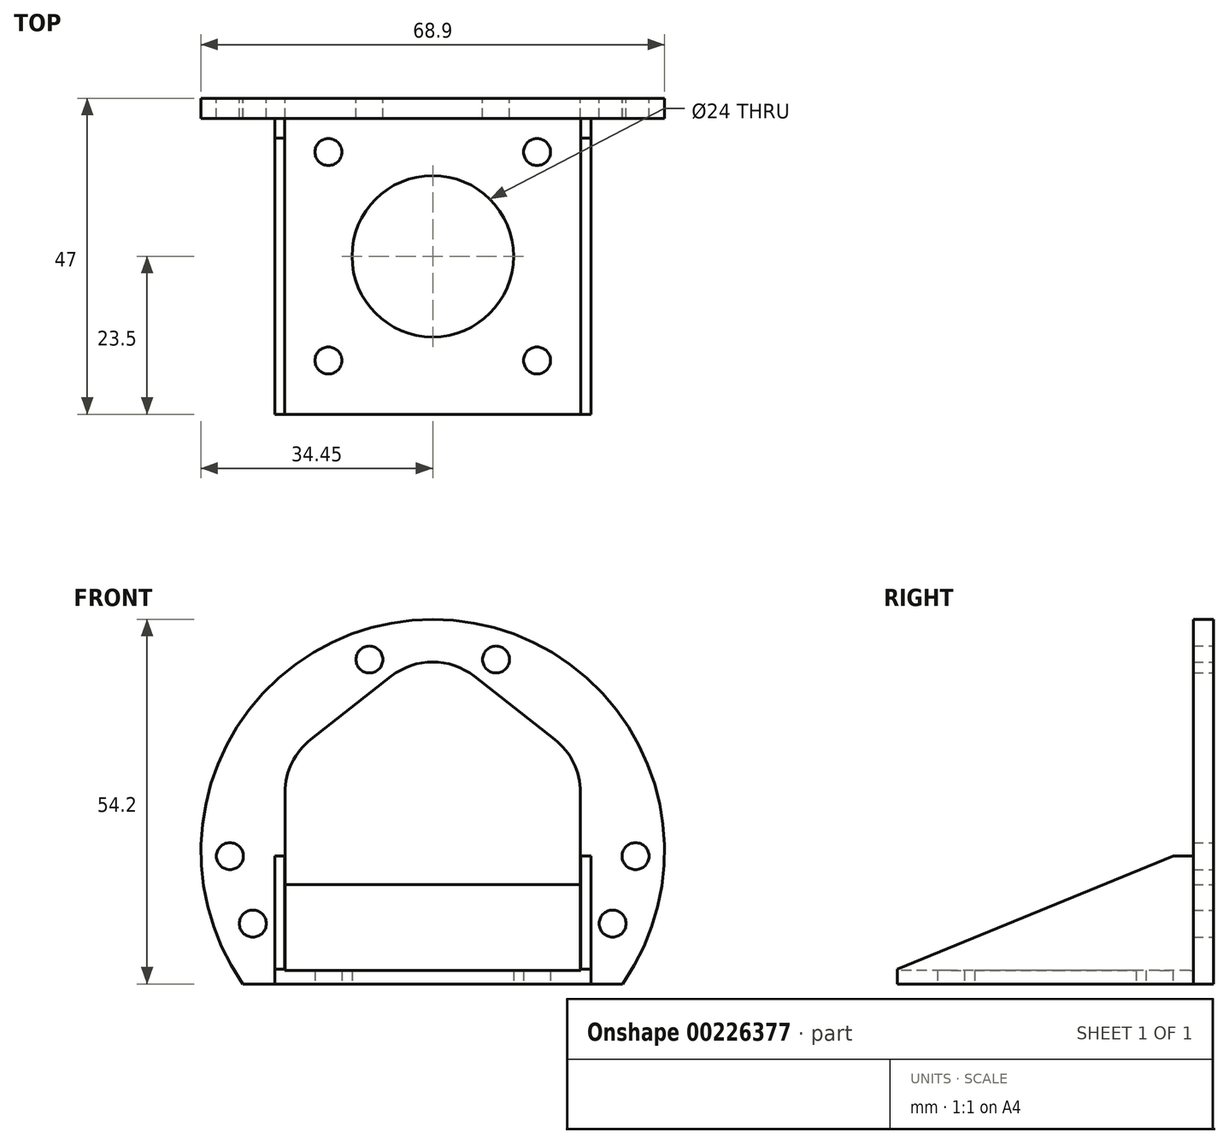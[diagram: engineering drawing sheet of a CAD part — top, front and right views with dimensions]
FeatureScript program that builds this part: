
annotation { "Feature Type Name" : "Feature", "Feature Type Description" : "" }
export const myFeature = defineFeature(function(context is Context, id is Id, definition is map)
    precondition{}
    {
        {
            var Q0;
            Q0=qCreatedBy(makeId("Top.planeOp"),FACE);
            var sketch = newSketch(context, id + "F0", { "sketchPlane" : qUnion([Q0])});
            skLineSegment(sketch, "E0.bottom", {"start": v(23.5, 23.5) * mm, "end": v(-23.5, 23.5) * mm});
            skLineSegment(sketch, "E0.top", {"start": v(23.5, -23.5) * mm, "end": v(-23.5, -23.5) * mm});
            skLineSegment(sketch, "E0.left", {"start": v(23.5, 23.5) * mm, "end": v(23.5, -23.5) * mm});
            skLineSegment(sketch, "E0.right", {"start": v(-23.5, 23.5) * mm, "end": v(-23.5, -23.5) * mm});
            skPoint(sketch, "E0.middle", {"position": v(0, 0) * mm});
            skLineSegment(sketch, "E1.bottom", {"start": v(15.5, 15.5) * mm, "end": v(-15.5, 15.5) * mm, "construction": true});
            skLineSegment(sketch, "E1.top", {"start": v(15.5, -15.5) * mm, "end": v(-15.5, -15.5) * mm, "construction": true});
            skLineSegment(sketch, "E1.left", {"start": v(15.5, 15.5) * mm, "end": v(15.5, -15.5) * mm, "construction": true});
            skLineSegment(sketch, "E1.right", {"start": v(-15.5, 15.5) * mm, "end": v(-15.5, -15.5) * mm, "construction": true});
            skCircle(sketch, "E2", {"center": v(0, 0) * mm, "radius": 12 * mm});
            skLineSegment(sketch, "E3.0", {"start": v(-22, 22) * mm, "end": v(-22, -23.5) * mm});
            skLineSegment(sketch, "E3.1", {"start": v(22, 22) * mm, "end": v(-22, 22) * mm});
            skLineSegment(sketch, "E3.2", {"start": v(22, 22) * mm, "end": v(22, -23.5) * mm});
            skSolve(sketch);
        }
        {
            var Q0;
            Q0=makeQuery(id+"F0.imprint","IMPRINT",FACE,{"disambiguationData":[TD([[makeQuery(id+"F0.imprint","IMPRINT",EDGE,{"derivedFrom":sQuery(id+"F0.wireOp",EDGE,"E0.bottom")}),1.0]])]});
            extrude(context, id + "F1", {"entities" : qUnion([Q0]), "depth" : 19 * mm});
        }
        {
            var Q0;
            Q0=makeQuery(id+"F0.imprint","IMPRINT",FACE,{"disambiguationData":[TD([[makeQuery(id+"F0.imprint","IMPRINT",EDGE,{"derivedFrom":sQuery(id+"F0.wireOp",EDGE,"E2")}),-1.0]])]});
            extrude(context, id + "F2", {"entities" : qUnion([Q0]), "operationType" : NewBodyOperationType.ADD, "depth" : 2 * mm});
        }
        {
            var Q0;
            Q0=sQuery(id+"F0.wireOp",VERTEX,"E1.right.start");
            var Q1;
            Q1=sQuery(id+"F0.wireOp",VERTEX,"E1.left.start");
            var Q2;
            Q2=sQuery(id+"F0.wireOp",VERTEX,"E1.left.end");
            var Q3;
            Q3=sQuery(id+"F0.wireOp",VERTEX,"E1.top.end");
            var Q4;
            Q4=makeQuery(id+"F1.opExtrude","SWEPT_BODY",BODY,{"disambiguationData":[OSD([sQuery(id+"F0.wireOp",EDGE,"E0.bottom"),sQuery(id+"F0.wireOp",EDGE,"E0.top"),sQuery(id+"F0.wireOp",EDGE,"E0.left"),sQuery(id+"F0.wireOp",EDGE,"E0.right"),sQuery(id+"F0.wireOp",EDGE,"E2")])]});
            hole(context, id + "F3", {"style" : HoleStyle.SIMPLE, "endStyle" : HoleEndStyle.THROUGH, "oppositeDirection" : true, "holeDiameter" : (4) * mm, "startFromSketch" : true, "locations" : qUnion([Q0, Q1, Q2, Q3]), "scope" : qUnion([Q4]), "isTappedThrough" : true});
        }
        {
            var Q0;
            Q0=makeQuery(id+"F1.opExtrude","SWEPT_FACE",FACE,{"disambiguationData":[OSD([sQuery(id+"F0.wireOp",EDGE,"E0.left")])]});
            var sketch = newSketch(context, id + "F4", { "sketchPlane" : qUnion([Q0])});
            skLineSegment(sketch, "E4", {"start": v(-23.5, 2.18) * mm, "end": v(17.57, 19) * mm});
            skLineSegment(sketch, "E5", {"start": v(17.57, 19) * mm, "end": v(-23.5, 19) * mm});
            skLineSegment(sketch, "E6", {"start": v(-23.5, 19) * mm, "end": v(-23.5, 2.18) * mm});
            skSolve(sketch);
        }
        {
            var Q0;
            Q0=makeQuery(id+"F4.imprint","IMPRINT",FACE,{"disambiguationData":[TD([[makeQuery(id+"F4.imprint","IMPRINT",EDGE,{"derivedFrom":sQuery(id+"F4.wireOp",EDGE,"E4")}),1.0]])]});
            extrude(context, id + "F5", {"entities" : qUnion([Q0]), "operationType" : NewBodyOperationType.REMOVE, "oppositeDirection" : true, "depth" : 50 * mm});
        }
        {
            var Q0;
            Q0=makeQuery(id+"F1.opExtrude","SWEPT_FACE",FACE,{"disambiguationData":[OSD([sQuery(id+"F0.wireOp",EDGE,"E0.bottom")])]});
            var sketch = newSketch(context, id + "F6", { "sketchPlane" : qUnion([Q0])});
            skLineSegment(sketch, "E7.bottom", {"start": v(-25.14, 19) * mm, "end": v(24.09, 19) * mm});
            skLineSegment(sketch, "E7.top", {"start": v(-25.14, 0) * mm, "end": v(24.09, 0) * mm});
            skLineSegment(sketch, "E7.left", {"start": v(-30.14, 14) * mm, "end": v(-30.14, 5) * mm});
            skLineSegment(sketch, "E7.right", {"start": v(29.09, 14) * mm, "end": v(29.09, 5) * mm});
            skPoint(sketch, "E8", {"position": v(-26.74, 8.97) * mm});
            skPoint(sketch, "E9", {"position": v(28.26, 9.5) * mm});
            skPoint(sketch, "E9.positionSnap0", {"position": v(23.5, 9.5) * mm});
            skPoint(sketch, "E10.visualSharp", {"position": v(-30.14, 19) * mm});
            skArc(sketch, "E10.filletArc", {"start": v(-25.14, 19) * mm, "mid": v(-28.68, 17.54) * mm, "end": v(-30.14, 14) * mm});
            skPoint(sketch, "E11.visualSharp", {"position": v(-30.14, 0) * mm});
            skArc(sketch, "E11.filletArc", {"start": v(-30.14, 5) * mm, "mid": v(-28.68, 1.46) * mm, "end": v(-25.14, 0) * mm});
            skPoint(sketch, "E12.visualSharp", {"position": v(29.09, 19) * mm});
            skArc(sketch, "E12.filletArc", {"start": v(29.09, 14) * mm, "mid": v(27.62, 17.54) * mm, "end": v(24.09, 19) * mm});
            skPoint(sketch, "E13.visualSharp", {"position": v(29.09, 0) * mm});
            skArc(sketch, "E13.filletArc", {"start": v(24.09, 0) * mm, "mid": v(27.62, 1.46) * mm, "end": v(29.09, 5) * mm});
            skPoint(sketch, "E14.MirrorP", {"position": v(30.14, 19) * mm});
            skPoint(sketch, "E15.MirrorP", {"position": v(26.74, 8.97) * mm});
            skSolve(sketch);
        }
        {
            var Q0;
            Q0=makeQuery(id+"F6.imprint","IMPRINT",FACE,{"disambiguationData":[TD([[makeQuery(id+"F6.imprint","IMPRINT",EDGE,{"derivedFrom":sQuery(id+"F6.wireOp",EDGE,"E7.left")}),1.0]])]});
            var Q1;
            Q1=makeQuery(id+"F6.imprint","IMPRINT",FACE,{"disambiguationData":[TD([[makeQuery(id+"F6.imprint","IMPRINT",EDGE,{"derivedFrom":sQuery(id+"F6.wireOp",EDGE,"E7.right")}),-1.0]])]});
            extrude(context, id + "F7", {"entities" : qUnion([Q0, Q1]), "operationType" : NewBodyOperationType.ADD, "oppositeDirection" : true, "depth" : 3 * mm});
        }
        {
            var Q0;
            Q0=sQuery(id+"F6.wireOp",VERTEX,"E8");
            var Q1;
            Q1=sQuery(id+"F6.wireOp",VERTEX,"E9");
            var Q2;
            Q2=makeQuery(id+"F1.opExtrude","SWEPT_BODY",BODY,{"disambiguationData":[OSD([sQuery(id+"F0.wireOp",EDGE,"E0.bottom"),sQuery(id+"F0.wireOp",EDGE,"E0.top"),sQuery(id+"F0.wireOp",EDGE,"E0.left"),sQuery(id+"F0.wireOp",EDGE,"E0.right"),sQuery(id+"F0.wireOp",EDGE,"E3.0"),sQuery(id+"F0.wireOp",EDGE,"E3.1"),sQuery(id+"F0.wireOp",EDGE,"E3.2")])]});
            hole(context, id + "F8", {"style" : HoleStyle.SIMPLE, "endStyle" : HoleEndStyle.THROUGH, "holeDiameter" : (4) * mm, "startFromSketch" : true, "locations" : qUnion([Q0, Q1]), "scope" : qUnion([Q2]), "isTappedThrough" : true});
        }
        {
            var Q0;
            Q0=makeQuery(id+"F1.opExtrude","SWEPT_EDGE",EDGE,{"disambiguationData":[OSD([sQuery(id+"F0.wireOp",EDGE,"E3.1"),sQuery(id+"F0.wireOp",EDGE,"E3.2")])]});
            var Q1;
            Q1=makeQuery(id+"F1.opExtrude","SWEPT_EDGE",EDGE,{"disambiguationData":[OSD([sQuery(id+"F0.wireOp",EDGE,"E3.0"),sQuery(id+"F0.wireOp",EDGE,"E3.1")])]});
            fillet(context, id + "F9", {"entities" : qUnion([Q0, Q1]), "radius" : 2 * mm, "tangentPropagation" : true, "allowEdgeOverflow" : false});
        }
        {
            var Q0;
            {var subQ1=sQuery(id+"F0.wireOp",EDGE,"E0.bottom");var subQ2=makeQuery(id+"F1.opExtrude","SWEPT_EDGE",EDGE,{"disambiguationData":[OSD([subQ1,sQuery(id+"F0.wireOp",EDGE,"E0.left")])]});Q0=makeQuery(id+"F6.imprint","IMPRINT",FACE,{"disambiguationData":[TD([[makeQuery(id+"F6.imprint","IMPRINT",EDGE,{"derivedFrom":subQ2}),1.0]])]});}
            var sketch = newSketch(context, id + "F10", { "sketchPlane" : qUnion([Q0])});
            skCircle(sketch, "E16", {"center": v(0, 19.75) * mm, "radius": 34.45 * mm});
            skSolve(sketch);
        }
        {
            var Q0;
            Q0=makeQuery(id+"F10.imprint","IMPRINT",FACE,{"disambiguationData":[TD([[makeQuery(id+"F10.imprint","IMPRINT",EDGE,{"derivedFrom":sQuery(id+"F10.wireOp",EDGE,"E16")}),1.0]])]});
            var Q1;
            {var subQ1=sQuery(id+"F0.wireOp",EDGE,"E0.bottom");var subQ2=makeQuery(id+"F1.opExtrude","SWEPT_EDGE",EDGE,{"disambiguationData":[OSD([subQ1,sQuery(id+"F0.wireOp",EDGE,"E0.left")])]});Q1=makeQuery(id+"F6.imprint","IMPRINT",FACE,{"disambiguationData":[TD([[makeQuery(id+"F6.imprint","IMPRINT",EDGE,{"derivedFrom":subQ2}),1.0]])]});}
            extrude(context, id + "F11", {"entities" : qUnion([Q0, Q1]), "operationType" : NewBodyOperationType.ADD, "oppositeDirection" : true, "depth" : 3 * mm});
        }
        {
            var Q0;
            {var subQ0=sQuery(id+"F6.wireOp",EDGE,"E7.top");var subQ1=sQuery(id+"F6.wireOp",EDGE,"E7.bottom");var subQ2=sQuery(id+"F0.wireOp",EDGE,"E0.right");var subQ3=sQuery(id+"F0.wireOp",EDGE,"E0.left");var subQ4=sQuery(id+"F0.wireOp",EDGE,"E0.bottom");Q0=makeQuery(id+"F11.boolean.opBoolean","MERGE",FACE,{"derivedFrom":[makeQuery(id+"F7.boolean.opBoolean","MERGE",FACE,{"derivedFrom":[makeQuery(id+"F1.opExtrude","SWEPT_FACE",FACE,{"disambiguationData":[OSD([subQ4])]}),makeQuery(id+"F7.opExtrude","CAP_FACE",FACE,{"disambiguationData":[OSD([subQ4,subQ3,subQ1,subQ0,sQuery(id+"F6.wireOp",EDGE,"E7.left"),sQuery(id+"F6.wireOp",EDGE,"E10.filletArc"),sQuery(id+"F6.wireOp",EDGE,"E11.filletArc")])],"isStart":true}),makeQuery(id+"F7.opExtrude","CAP_FACE",FACE,{"disambiguationData":[OSD([subQ4,subQ2,subQ1,subQ0,sQuery(id+"F6.wireOp",EDGE,"E7.right"),sQuery(id+"F6.wireOp",EDGE,"E12.filletArc"),sQuery(id+"F6.wireOp",EDGE,"E13.filletArc")])],"isStart":true})]}),makeQuery(id+"F11.opExtrude","CAP_FACE",FACE,{"disambiguationData":[OSD([subQ4,subQ3,subQ2,subQ1,subQ0])],"isStart":true}),makeQuery(id+"F11.opExtrude","CAP_FACE",FACE,{"disambiguationData":[OSD([subQ4,subQ3,subQ2,subQ1,subQ0,sQuery(id+"F10.wireOp",EDGE,"E16")])],"isStart":true})]});}
            var sketch = newSketch(context, id + "F12", { "sketchPlane" : qUnion([Q0])});
            skLineSegment(sketch, "E17", {"start": v(-21.94, 28.5) * mm, "end": v(-21.94, 14.76) * mm});
            skLineSegment(sketch, "E18", {"start": v(-21.94, 14.76) * mm, "end": v(21.94, 14.76) * mm});
            skLineSegment(sketch, "E19", {"start": v(21.94, 14.76) * mm, "end": v(21.94, 28.5) * mm});
            skLineSegment(sketch, "E20", {"start": v(18.1, 36.38) * mm, "end": v(6.17, 45.74) * mm});
            skLineSegment(sketch, "E21", {"start": v(-6.17, 45.74) * mm, "end": v(-18.1, 36.38) * mm});
            skPoint(sketch, "E22.visualSharp", {"position": v(0, 50.59) * mm});
            skArc(sketch, "E22.filletArc", {"start": v(6.17, 45.74) * mm, "mid": v(0, 47.88) * mm, "end": v(-6.17, 45.74) * mm});
            skPoint(sketch, "E23.visualSharp", {"position": v(21.94, 33.37) * mm});
            skArc(sketch, "E23.filletArc", {"start": v(21.94, 28.5) * mm, "mid": v(20.93, 32.88) * mm, "end": v(18.1, 36.38) * mm});
            skPoint(sketch, "E24.visualSharp", {"position": v(-21.94, 33.37) * mm});
            skArc(sketch, "E24.filletArc", {"start": v(-18.1, 36.38) * mm, "mid": v(-20.93, 32.88) * mm, "end": v(-21.94, 28.5) * mm});
            skPoint(sketch, "E25.end.orphan", {"position": v(-28.22, 0) * mm});
            skPoint(sketch, "E25.start.orphan", {"position": v(28.22, 0) * mm});
            skLineSegment(sketch, "E26", {"start": v(-28.22, 0) * mm, "end": v(28.22, 0) * mm});
            skPoint(sketch, "E27", {"position": v(-9.4, 48.24) * mm});
            skPoint(sketch, "E28.MirrorP", {"position": v(9.4, 48.24) * mm});
            skSolve(sketch);
        }
        {
            var Q0;
            {var subQ0=sQuery(id+"F12.wireOp",EDGE,"E25");Q0=makeQuery(id+"F12.imprint","IMPRINT",FACE,{"disambiguationData":[TD([[makeQuery(id+"F12.imprint","IMPRINT",EDGE,{"derivedFrom":subQ0}),1.0]])]});}
            var Q1;
            Q1=makeQuery(id+"F12.imprint","IMPRINT",FACE,{"disambiguationData":[TD([[makeQuery(id+"F12.imprint","IMPRINT",EDGE,{"derivedFrom":sQuery(id+"F12.wireOp",EDGE,"E17")}),1.0]])]});
            var Q2;
            {var subQ0=sQuery(id+"F12.wireOp",EDGE,"E26");Q2=makeQuery(id+"F12.imprint","IMPRINT",FACE,{"disambiguationData":[TD([[makeQuery(id+"F12.imprint","IMPRINT",EDGE,{"derivedFrom":subQ0}),-1.0]])]});}
            extrude(context, id + "F13", {"entities" : qUnion([Q0, Q1, Q2]), "operationType" : NewBodyOperationType.REMOVE, "oppositeDirection" : true, "depth" : 25 * mm});
        }
        {
            var Q0;
            Q0=sQuery(id+"F6.wireOp",VERTEX,"E10.visualSharp");
            var Q1;
            Q1=sQuery(id+"F6.wireOp",VERTEX,"E8");
            var Q2;
            Q2=sQuery(id+"F12.wireOp",VERTEX,"E28.MirrorP");
            var Q3;
            Q3=sQuery(id+"F12.wireOp",VERTEX,"E27");
            var Q4;
            Q4=sQuery(id+"F6.wireOp",VERTEX,"E15.MirrorP");
            var Q5;
            Q5=sQuery(id+"F6.wireOp",VERTEX,"E14.MirrorP");
            var Q6;
            Q6=makeQuery(id+"F1.opExtrude","SWEPT_BODY",BODY,{"disambiguationData":[OSD([sQuery(id+"F0.wireOp",EDGE,"E0.bottom"),sQuery(id+"F0.wireOp",EDGE,"E0.top"),sQuery(id+"F0.wireOp",EDGE,"E0.left"),sQuery(id+"F0.wireOp",EDGE,"E0.right"),sQuery(id+"F0.wireOp",EDGE,"E3.0"),sQuery(id+"F0.wireOp",EDGE,"E3.1"),sQuery(id+"F0.wireOp",EDGE,"E3.2")])]});
            hole(context, id + "F14", {"style" : HoleStyle.SIMPLE, "endStyle" : HoleEndStyle.BLIND, "holeDiameter" : 4 * mm, "holeDepth" : 6 * mm, "startFromSketch" : true, "locations" : qUnion([Q0, Q1, Q2, Q3, Q4, Q5]), "scope" : qUnion([Q6])});
        }
    });
